# Revit family: RAS-J2AVSG1_10-16_Outdoor Unit
name_source: partatom
category: Mechanical Equipment
revit_build: Autodesk Revit 2017 (Build: 20160225_1515(x64)
units: mm (PartAtom-declared; Revit-internal decimal feet)

## family parameters
Always vertical = Yes
Cut with Voids When Loaded = No
OmniClass Number = 23.75.00.00
OmniClass Title = Climate Control (HVAC)
Part Type = Normal
Room Calculation Point = No
Round Connector Dimension = Use Diameter
Shared = No
Work Plane-Based = No

## types (3) — shared parameters
Article Description = Haori desing tier
Back Clearance (mm) (default) = 100 mm  [stored 0.328084 ft]
Compressor detail - Motor output  (W) = -
Compressor detail - Type = Hermetic DC rotary compressor
Content Supplier URL = www.hcltech.com
Custom = No
Depth (mm) = 290 mm
Description = Haori desing tier
Drain pipe(mm) = -
Duct diameters(mm) = -
EMCS = 4
ETIM Article Class = EC001213
Energy class-Cooling/Heating = A+++ / A+++
Family Version = 2017
Frequency (Hz) = 50Hz
Front Clearance (mm) (default) = 600 mm  [stored 1.9685 ft]
Height (mm) = 550 mm  [stored 1.80446 ft]
Left Side Clearance (mm) (default) = 100 mm  [stored 0.328084 ft]
MCA (A) = -
MEPcontent Class = HEATPUMP
MOCP (A) = 15
Manufacturer = Toshiba
Manufacturer URL = https://www.toshiba-carrier.co.jp
Operating range - Cooling (°C) = -15 - 46
Operating range - Heating (°C) = -15- 24
Pdesigh-Cooling/Heating = -
Piping diameter (mm)-Liquid = 6 mm  [stored 0.019685 ft]
Product Line = TCTC
Red = Colour RGB-255 000 000
Refrigerant information = R32
Right Side Clearance (mm) (default) = 600 mm  [stored 1.9685 ft]
Sound pressure dB(A)-Cooling/Heating-Low = -
Sound pressure dB(A)-Cooling/Heating-Low+ = -
Sound pressure dB(A)-Cooling/Heating-Mid = -
Sound pressure dB(A)-Cooling/Heating-Mid+ = -
Starting current = -
Static pressure = -
Top Clearance (mm) (default) = 600 mm  [stored 1.9685 ft]
URL = https://www.toshiba-carrier.co.jp
Voltage (V) = 220-240V
White = Colour RGB-255 255 255
Width (mm) = 780 mm  [stored 2.55906 ft]

## per-type parameters (varying)
| type | Airflow m3/h-Cooling/Heating | Model | Piping diameter (mm)-Gas | Power consumption-Cooling | Power consumption-Heating | Rated Capacity kW-Cooling/Heating | Rated Power Consumption kW-Cooling/Heating | Rated efficiency-EER / COP | Running current-Cooling | Running current-Heating | Seasonal Efficiency-SEER  / SCOP | Sound pressure dB(A)-Cooling/Heating-High | Weight (Kg) |
| RAS-10J2AVSG-E1 | 1890 / 1890 | RAS-07J2AVSG-E | 10 mm  [stored 0.0328084 ft] | 505 | 705 | 2.5 / 3.2 | 0.54 / 0.74 | 4.63 / 4.32 | 2.57 - 2.35 | 3.30 - 3.02 | 8.60 / 5.10 | 46 / 48 | 26 |
| RAS-13J2AVSG-E1 | 1950 / 1950 | RAS-13J2AVSG-E1 | 10 mm  [stored 0.0328084 ft] | 760 | 1040 | 3.5 / 4.2 | 0.80 / 1.08 | 4.38 / 3.89 | 4.23 - 3.86 | 4.92 - 4.54 | 8.60 / 5.10 | 46 / 48 | 30 |
| RAS-16J2AVSG-E1 | 2040 / 2040 | RAS-16J2AVSG-E1 | 13 mm | 1305 | 1475 | 4.6 / 5.5 | 1.35 / 1.52 | 3.41 / 3.62 | 6.41 - 5.91 | 7.04 - 6.46 | 7.80 / 4.60 | 48 / 50 | 33 |

note: column(s) folded — value = type name in every type: Article Type, Manufacturer Art. No.

note: [stored X ft] marks values corroborated as IEEE doubles in the binary element streams (Revit-internal decimal feet)

## geometry (parser evidence)
native form markers: Sweep x8
no freeform markers — native parametric forms only
